# Revit family: Artemide_Vector_PendantMagnetic
name_source: partatom
category: Lighting Fixtures
revit_build: Autodesk Revit 2018 (Build: 20190510_1515(x64)
units: mm (PartAtom-declared; Revit-internal decimal feet)

## family parameters
Always vertical = Yes
Cut with Voids When Loaded = No
Light Source = No
Part Type = Normal
Room Calculation Point = No
Round Connector Dimension = Use Diameter
Shared = No
Work Plane-Based = Yes

## types (135) — shared parameters
6 Monthly = -
Air Handling = -
Annually = -
Application Environment = Internal
Beam Angle Longditudinal Axis  = 0.00°
Beam Angle Transverse Axis  = 0.00°
Bespoke Timeframe = -
CE Approval = Y
Cable Material = -
Colour Rendering Index = 90
Column = -
Control Gear Location = -
Control Gear Required = -
Control Gear Type = -
Daily = -
Daylight Sensor = -
Default Elevation = 1219 mm
Diffuser Finish = -
Diffuser Material  = -
Diffusing screen = -
Distance_HeightTrack = 19 mm
Distance_LeftEndTrack = 54 mm
Distance_RightEnd Track = 54 mm
Distance_WidthTrack = 24 mm
ENEC Certification of European conformity = N
Earth Point  = -
Emergency = N
Emergency Lighting Battery = -
End Caps/Transition Caps/Joints = -
Environmental Product Declaration = -
Expected Life = -
Face Shape = Cylindrical
Features = -
Fire Rated = -
Fire Shroud = -
Fixing Material = -
Fixings = -
Gasket Material = -
Green Guide for Specification = -
Hazardous Area Category = -
Hazardous Area Protection Type = -
Housing Finish  = Painted
Housing Material = Aluminum
IES Files  = -
IK Rating = -
IP Rating = IP20
IfcExportAs = IfcLightFixtureType
IfcExportType = NOT DEFINED
Infills = -
Integral Emergency Lighting Battery Type = -
Integral Fuse or Circuit Protection  = -
Intended Market = Unset
International Type Code = -
Lamp Cap = LED Integrated
Lamp Holder Material = -
Lamp Included = Y
Lamp Replacement Interval = -
Lamp Survival Factor = -
Life Cycle Analysis = -
Light Fixture Mounting Type = Suspended
Light Output Pattern = -
Location of Manufacturer = -
Louvre/Lens = -
Luminaire Cleaning Interval  = -
Luminaire Type = Floodlight
M_Diffuser = Artemide_Glass_LightBulb
Maintenance Required: 0-300hrs  = -
Maintenance Required: 1001-2000hrs  = -
Maintenance Required: 2001-4000hrs  = -
Maintenance Required: 301-600hrs  = -
Maintenance Required: 4001-8000hrs  = -
Maintenance Required: 601-1000hrs = -
Maintenance Required: 8001-12000hrs  = -
Manufacturer = Artemide
Manufacturer Website = https://www.artemide.com
Material Ingredient Reporting = -
Max Height from ceiling = 2000 mm  [stored 6.56168 ft]
Monthly = -
Motion Detector = -
Motion Sensor = -
Number of Primary Lamps = 1
Photocell = -
Power Supply Kit = -
Primary Lamp Type = LED
Product Literature = https://www.artemide.com
Product Range = Vector
Quarterly = -
Reflector Finish = -
Reflector Material = -
Responsible Extraction of Materials = -
Responsible Sourcing of Materials = -
Secondary Lamp = N
Secondary Lamp Cap = -
Secondary Lamp Included = -
Secondary Lamp International Type Code = -
Service life  = -
Standards = -
Suitable Dimmer Type = DALI
Suitable for Dimming  = Y
Suitable for Motion Detector Control = N
Suitable for Photocell Control = -
Testing method = -
Trim Colour  = -
Trim Finish = -
Trim Material = -
URL to Energy Technology List = -
URL to O&M Manual = -
Uniclass 2015 = Pr_70_70_48
Unified Glare Rating  = -
Voltage = -
Warranty ID = https://cloud.artemide.com
Weekly = -
zero-valued in all types: Access Clearance Bottom, Access Clearance Front, Access Clearance Left, Access Clearance Rear, Access Clearance Right, Access Clearance Top, Ambient Temperature                            , Basis of lifetime lumen depreciation  , Basis of lifetime luminaire failures       , Control Gear Standby Power , Current , Cut Out Length, Cut Out Width, Downward Component, Drive Current                                         , Duration of Integral Emergency Lighting , Efficiency, Embodied Carbon , Emergency Charging Power      , Emergency light output percentage, External Control Line Voltage, Face Length, Face Width, Fire Rated Temperature, Fire Rating Duration, Frequency , Gross Weight, Input Lumens Direct light, Input Lumens Indirect light, LED Initial Colour Variation                     , LED Maintained Colour Variation        , LED lifetime, Luminaire Maintenance Factor, Luminance at 65deg Angle, Maximum Operating Temperature, Minimum Operating Temperature, Number of Poles, Number of Secondary Lamps, Output Lumens Indirect light, Overall Light Output Ratio, Overall Width, Power Factor, Secondary Lamp Colour Rendering Index, Secondary Lamp Colour Temperature, Secondary Lamp Efficacy, Secondary Lamp Initial Lumens , Secondary Lamp Voltage, Secondary Rated Lamp Life, Shipping Weight, Supply Phase, Total Light Output , Total Power, Upward Component 

## per-type parameters (varying)
| type | Colour Temperature | Distance_HeightLamp | Housing Colour  | Initial Lumens | M_Fixings | M_Housing | M_TopCap | M_Track | Output Lumens Direct light | Overall Height | Overall Length | Product Model Number | Radius_Lamp | Rated Lamp Life | Wattage  |
| Vector_PendantMagnetic_30_16°_2700K_DALI_BrushedSilver_BN31115 | 2700 | 79 mm | Brushed Silver | 422 | Artemide_Aluminum_Black | Artemide_Aluminum_BrushedSilver | Artemide_Aluminum_BrushedSilver | Artemide_Aluminum_Black | 422 | 78 | 30 | BN31115 | 15 mm  [stored 0.0492126 ft] | 60500 | 6 |
| Vector_PendantMagnetic_40_13°_2700K_DALI_BrushedSilver_AP21115 | 2700 | 105 mm | Brushed Silver | 540 | Artemide_Aluminum_Black | Artemide_Aluminum_BrushedSilver | Artemide_Aluminum_BrushedSilver | Artemide_Aluminum_Black | 540 | 104 | 40 | AP21115 | 20 mm  [stored 0.0656168 ft] | 60500 | 10 |
| Vector_PendantMagnetic_55_16°_2700K_DALI_BrushedSilver_AP31115 | 2700 | 132 mm | Brushed Silver | 1492 | Artemide_Aluminum_Black | Artemide_Aluminum_BrushedSilver | Artemide_Aluminum_BrushedSilver | Artemide_Aluminum_Black | 1492 | 130 | 55 | AP31115 | 28 mm | 50000 | 26 |
| Vector_PendantMagnetic_30_16°_3000K_DALI_BrushedSilver_BN30115 | 3000 | 79 mm | Brushed Silver | 422 | Artemide_Aluminum_Black | Artemide_Aluminum_BrushedSilver | Artemide_Aluminum_BrushedSilver | Artemide_Aluminum_Black | 422 | 78 | 30 | BN30115 | 15 mm  [stored 0.0492126 ft] | 60500 | 6 |
| Vector_PendantMagnetic_30_16°_4000K_DALI_BrushedSilver_BN35115 | 4000 | 79 mm | Brushed Silver | 422 | Artemide_Aluminum_Black | Artemide_Aluminum_BrushedSilver | Artemide_Aluminum_BrushedSilver | Artemide_Aluminum_Black | 422 | 78 | 30 | BN35115 | 15 mm  [stored 0.0492126 ft] | 60500 | 6 |
| Vector_PendantMagnetic_30_20°_2700K_DALI_BrushedSilver_BN31215 | 2700 | 79 mm | Brushed Silver | 404 | Artemide_Aluminum_Black | Artemide_Aluminum_BrushedSilver | Artemide_Aluminum_BrushedSilver | Artemide_Aluminum_Black | 404 | 78 | 30 | BN31215 | 15 mm  [stored 0.0492126 ft] | 60500 | 6 |
| Vector_PendantMagnetic_30_20°_3000K_DALI_BrushedSilver_BN30215 | 3000 | 79 mm | Brushed Silver | 404 | Artemide_Aluminum_Black | Artemide_Aluminum_BrushedSilver | Artemide_Aluminum_BrushedSilver | Artemide_Aluminum_Black | 404 | 78 | 30 | BN30215 | 15 mm  [stored 0.0492126 ft] | 60500 | 6 |
| Vector_PendantMagnetic_30_20°_4000K_DALI_BrushedSilver_BN35215 | 4000 | 79 mm | Brushed Silver | 404 | Artemide_Aluminum_Black | Artemide_Aluminum_BrushedSilver | Artemide_Aluminum_BrushedSilver | Artemide_Aluminum_Black | 404 | 78 | 30 | BN35215 | 15 mm  [stored 0.0492126 ft] | 60500 | 6 |
| Vector_PendantMagnetic_30_28°_2700K_DALI_BrushedSilver_BN31315 | 2700 | 79 mm | Brushed Silver | 373 | Artemide_Aluminum_Black | Artemide_Aluminum_BrushedSilver | Artemide_Aluminum_BrushedSilver | Artemide_Aluminum_Black | 373 | 78 | 30 | BN31315 | 15 mm  [stored 0.0492126 ft] | 60500 | 6 |
| Vector_PendantMagnetic_30_28°_3000K_DALI_BrushedSilver_BN30315 | 3000 | 79 mm | Brushed Silver | 373 | Artemide_Aluminum_Black | Artemide_Aluminum_BrushedSilver | Artemide_Aluminum_BrushedSilver | Artemide_Aluminum_Black | 373 | 78 | 30 | BN30315 | 15 mm  [stored 0.0492126 ft] | 60500 | 6 |
| Vector_PendantMagnetic_30_28°_4000K_DALI_BrushedSilver_BN35315 | 4000 | 79 mm | Brushed Silver | 373 | Artemide_Aluminum_Black | Artemide_Aluminum_BrushedSilver | Artemide_Aluminum_BrushedSilver | Artemide_Aluminum_Black | 373 | 78 | 30 | BN35315 | 15 mm  [stored 0.0492126 ft] | 60500 | 6 |
| Vector_PendantMagnetic_30_16°_2700K_DALI_White_BN31101 | 2700 | 79 mm | White | 422 | Artemide_Aluminum_White | Artemide_Aluminum_White | Artemide_Aluminum_White | Artemide_Aluminum_White | 422 | 78 | 30 | BN31101 | 15 mm  [stored 0.0492126 ft] | 60500 | 6 |
| Vector_PendantMagnetic_30_16°_3000K_DALI_White_BN30101 | 3000 | 79 mm | White | 422 | Artemide_Aluminum_White | Artemide_Aluminum_White | Artemide_Aluminum_White | Artemide_Aluminum_White | 422 | 78 | 30 | BN30101 | 15 mm  [stored 0.0492126 ft] | 60500 | 6 |
| Vector_PendantMagnetic_30_16°_4000K_DALI_White_BN35101 | 4000 | 79 mm | White | 422 | Artemide_Aluminum_White | Artemide_Aluminum_White | Artemide_Aluminum_White | Artemide_Aluminum_White | 422 | 78 | 30 | BN35101 | 15 mm  [stored 0.0492126 ft] | 60500 | 6 |
| Vector_PendantMagnetic_30_20°_2700K_DALI_White_BN31201 | 2700 | 79 mm | White | 404 | Artemide_Aluminum_White | Artemide_Aluminum_White | Artemide_Aluminum_White | Artemide_Aluminum_White | 404 | 78 | 30 | BN31201 | 15 mm  [stored 0.0492126 ft] | 60500 | 6 |
| Vector_PendantMagnetic_30_20°_3000K_DALI_White_BN30201 | 3000 | 79 mm | White | 404 | Artemide_Aluminum_White | Artemide_Aluminum_White | Artemide_Aluminum_White | Artemide_Aluminum_White | 404 | 78 | 30 | BN30201 | 15 mm  [stored 0.0492126 ft] | 60500 | 6 |
| Vector_PendantMagnetic_30_20°_4000K_DALI_White_BN35201 | 4000 | 79 mm | White | 404 | Artemide_Aluminum_White | Artemide_Aluminum_White | Artemide_Aluminum_White | Artemide_Aluminum_White | 404 | 78 | 30 | BN35201 | 15 mm  [stored 0.0492126 ft] | 60500 | 6 |
| Vector_PendantMagnetic_30_28°_2700K_DALI_White_BN31301 | 2700 | 79 mm | White | 373 | Artemide_Aluminum_White | Artemide_Aluminum_White | Artemide_Aluminum_White | Artemide_Aluminum_White | 373 | 78 | 30 | BN31301 | 15 mm  [stored 0.0492126 ft] | 60500 | 6 |
| Vector_PendantMagnetic_30_28°_3000K_DALI_White_BN30301 | 3000 | 79 mm | White | 373 | Artemide_Aluminum_White | Artemide_Aluminum_White | Artemide_Aluminum_White | Artemide_Aluminum_White | 373 | 78 | 30 | BN30301 | 15 mm  [stored 0.0492126 ft] | 60500 | 6 |
| Vector_PendantMagnetic_30_28°_4000K_DALI_White_BN35301 | 4000 | 79 mm | White | 373 | Artemide_Aluminum_White | Artemide_Aluminum_White | Artemide_Aluminum_White | Artemide_Aluminum_White | 373 | 78 | 30 | BN35301 | 15 mm  [stored 0.0492126 ft] | 60500 | 6 |
| Vector_PendantMagnetic_30_16°_2700K_DALI_BrushedBronze_BN31120 | 2700 | 79 mm | Brushed Bronze | 422 | Artemide_Aluminum_Black | Artemide_Aluminum_BrushedBronze | Artemide_Aluminum_BrushedBronze | Artemide_Aluminum_Black | 422 | 78 | 30 | BN31120 | 15 mm  [stored 0.0492126 ft] | 60500 | 6 |
| Vector_PendantMagnetic_30_16°_3000K_DALI_BrushedBronze_BN30120 | 3000 | 79 mm | Brushed Bronze | 422 | Artemide_Aluminum_Black | Artemide_Aluminum_BrushedBronze | Artemide_Aluminum_BrushedBronze | Artemide_Aluminum_Black | 422 | 78 | 30 | BN30120 | 15 mm  [stored 0.0492126 ft] | 60500 | 6 |
| Vector_PendantMagnetic_30_16°_4000K_DALI_BrushedBronze_BN35120 | 4000 | 79 mm | Brushed Bronze | 422 | Artemide_Aluminum_Black | Artemide_Aluminum_BrushedBronze | Artemide_Aluminum_BrushedBronze | Artemide_Aluminum_Black | 422 | 78 | 30 | BN35120 | 15 mm  [stored 0.0492126 ft] | 60500 | 6 |
| Vector_PendantMagnetic_30_20°_2700K_DALI_BrushedBronze_BN31220 | 2700 | 79 mm | Brushed Bronze | 404 | Artemide_Aluminum_Black | Artemide_Aluminum_BrushedBronze | Artemide_Aluminum_BrushedBronze | Artemide_Aluminum_Black | 404 | 78 | 30 | BN31220 | 15 mm  [stored 0.0492126 ft] | 60500 | 6 |
| Vector_PendantMagnetic_30_20°_3000K_DALI_BrushedBronze_BN30220 | 3000 | 79 mm | Brushed Bronze | 404 | Artemide_Aluminum_Black | Artemide_Aluminum_BrushedBronze | Artemide_Aluminum_BrushedBronze | Artemide_Aluminum_Black | 404 | 78 | 30 | BN30220 | 15 mm  [stored 0.0492126 ft] | 60500 | 6 |
| Vector_PendantMagnetic_30_20°_4000K_DALI_BrushedBronze_BN35220 | 4000 | 79 mm | Brushed Bronze | 404 | Artemide_Aluminum_Black | Artemide_Aluminum_BrushedBronze | Artemide_Aluminum_BrushedBronze | Artemide_Aluminum_Black | 404 | 78 | 30 | BN35220 | 15 mm  [stored 0.0492126 ft] | 60500 | 6 |
| Vector_PendantMagnetic_30_28°_2700K_DALI_BrushedBronze_BN31320 | 2700 | 79 mm | Brushed Bronze | 373 | Artemide_Aluminum_Black | Artemide_Aluminum_BrushedBronze | Artemide_Aluminum_BrushedBronze | Artemide_Aluminum_Black | 373 | 78 | 30 | BN31320 | 15 mm  [stored 0.0492126 ft] | 60500 | 6 |
| Vector_PendantMagnetic_30_28°_3000K_DALI_BrushedBronze_BN30320 | 3000 | 79 mm | Brushed Bronze | 373 | Artemide_Aluminum_Black | Artemide_Aluminum_BrushedBronze | Artemide_Aluminum_BrushedBronze | Artemide_Aluminum_Black | 373 | 78 | 30 | BN30320 | 15 mm  [stored 0.0492126 ft] | 60500 | 6 |
| Vector_PendantMagnetic_30_28°_4000K_DALI_BrushedBronze_BN35320 | 4000 | 79 mm | Brushed Bronze | 373 | Artemide_Aluminum_Black | Artemide_Aluminum_BrushedBronze | Artemide_Aluminum_BrushedBronze | Artemide_Aluminum_Black | 373 | 78 | 30 | BN35320 | 15 mm  [stored 0.0492126 ft] | 60500 | 6 |
| Vector_PendantMagnetic_30_16°_2700K_DALI_Black_BN31104 | 2700 | 79 mm | Black | 422 | Artemide_Aluminum_Black | Artemide_Aluminum_Black | Artemide_Aluminum_Black | Artemide_Aluminum_Black | 422 | 78 | 30 | BN31104 | 15 mm  [stored 0.0492126 ft] | 60500 | 6 |
| Vector_PendantMagnetic_30_16°_3000K_DALI_Black_BN30104 | 3000 | 79 mm | Black | 422 | Artemide_Aluminum_Black | Artemide_Aluminum_Black | Artemide_Aluminum_Black | Artemide_Aluminum_Black | 422 | 78 | 30 | BN30104 | 15 mm  [stored 0.0492126 ft] | 60500 | 6 |
| Vector_PendantMagnetic_30_16°_4000K_DALI_Black_BN35104 | 4000 | 79 mm | Black | 422 | Artemide_Aluminum_Black | Artemide_Aluminum_Black | Artemide_Aluminum_Black | Artemide_Aluminum_Black | 422 | 78 | 30 | BN35104 | 15 mm  [stored 0.0492126 ft] | 60500 | 6 |
| Vector_PendantMagnetic_30_20°_2700K_DALI_Black_BN31204 | 2700 | 79 mm | Black | 404 | Artemide_Aluminum_Black | Artemide_Aluminum_Black | Artemide_Aluminum_Black | Artemide_Aluminum_Black | 404 | 78 | 30 | BN31204 | 15 mm  [stored 0.0492126 ft] | 60500 | 6 |
| Vector_PendantMagnetic_30_20°_3000K_DALI_Black_BN30204 | 3000 | 79 mm | Black | 404 | Artemide_Aluminum_Black | Artemide_Aluminum_Black | Artemide_Aluminum_Black | Artemide_Aluminum_Black | 404 | 78 | 30 | BN30204 | 15 mm  [stored 0.0492126 ft] | 60500 | 6 |
| Vector_PendantMagnetic_30_20°_4000K_DALI_Black_BN35204 | 4000 | 79 mm | Black | 404 | Artemide_Aluminum_Black | Artemide_Aluminum_Black | Artemide_Aluminum_Black | Artemide_Aluminum_Black | 404 | 78 | 30 | BN35204 | 15 mm  [stored 0.0492126 ft] | 60500 | 6 |
| Vector_PendantMagnetic_30_28°_2700K_DALI_Black_BN31304 | 2700 | 79 mm | Black | 373 | Artemide_Aluminum_Black | Artemide_Aluminum_Black | Artemide_Aluminum_Black | Artemide_Aluminum_Black | 373 | 78 | 30 | BN31304 | 15 mm  [stored 0.0492126 ft] | 60500 | 6 |
| Vector_PendantMagnetic_30_28°_3000K_DALI_Black_BN30304 | 3000 | 79 mm | Black | 373 | Artemide_Aluminum_Black | Artemide_Aluminum_Black | Artemide_Aluminum_Black | Artemide_Aluminum_Black | 373 | 78 | 30 | BN30304 | 15 mm  [stored 0.0492126 ft] | 60500 | 6 |
| Vector_PendantMagnetic_30_28°_4000K_DALI_Black_BN35304 | 4000 | 79 mm | Black | 373 | Artemide_Aluminum_Black | Artemide_Aluminum_Black | Artemide_Aluminum_Black | Artemide_Aluminum_Black | 373 | 78 | 30 | BN35304 | 15 mm  [stored 0.0492126 ft] | 60500 | 6 |
| Vector_PendantMagnetic_30_16°_2700K_DALI_BrushedCopper_BN31118 | 2700 | 79 mm | Brushed Copper | 422 | Artemide_Aluminum_Black | Artemide_Aluminum_BrushedCopper | Artemide_Aluminum_BrushedCopper | Artemide_Aluminum_Black | 422 | 78 | 30 | BN31118 | 15 mm  [stored 0.0492126 ft] | 60500 | 6 |
| Vector_PendantMagnetic_30_16°_3000K_DALI_BrushedCopper_BN30118 | 3000 | 79 mm | Brushed Copper | 422 | Artemide_Aluminum_Black | Artemide_Aluminum_BrushedCopper | Artemide_Aluminum_BrushedCopper | Artemide_Aluminum_Black | 422 | 78 | 30 | BN30118 | 15 mm  [stored 0.0492126 ft] | 60500 | 6 |
| Vector_PendantMagnetic_30_16°_4000K_DALI_BrushedCopper_BN35118 | 4000 | 79 mm | Brushed Copper | 422 | Artemide_Aluminum_Black | Artemide_Aluminum_BrushedCopper | Artemide_Aluminum_BrushedCopper | Artemide_Aluminum_Black | 422 | 78 | 30 | BN35118 | 15 mm  [stored 0.0492126 ft] | 60500 | 6 |
| Vector_PendantMagnetic_30_20°_2700K_DALI_BrushedCopper_BN31218 | 2700 | 79 mm | Brushed Copper | 404 | Artemide_Aluminum_Black | Artemide_Aluminum_BrushedCopper | Artemide_Aluminum_BrushedCopper | Artemide_Aluminum_Black | 404 | 78 | 30 | BN31218 | 15 mm  [stored 0.0492126 ft] | 60500 | 6 |
| Vector_PendantMagnetic_30_20°_3000K_DALI_BrushedCopper_BN30218 | 3000 | 79 mm | Brushed Copper | 404 | Artemide_Aluminum_Black | Artemide_Aluminum_BrushedCopper | Artemide_Aluminum_BrushedCopper | Artemide_Aluminum_Black | 404 | 78 | 30 | BN30218 | 15 mm  [stored 0.0492126 ft] | 60500 | 6 |
| Vector_PendantMagnetic_30_20°_4000K_DALI_BrushedCopper_BN35218 | 4000 | 79 mm | Brushed Copper | 404 | Artemide_Aluminum_Black | Artemide_Aluminum_BrushedCopper | Artemide_Aluminum_BrushedCopper | Artemide_Aluminum_Black | 404 | 78 | 30 | BN35218 | 15 mm  [stored 0.0492126 ft] | 60500 | 6 |
| Vector_PendantMagnetic_30_28°_2700K_DALI_BrushedCopper_BN31318 | 2700 | 79 mm | Brushed Copper | 373 | Artemide_Aluminum_Black | Artemide_Aluminum_BrushedCopper | Artemide_Aluminum_BrushedCopper | Artemide_Aluminum_Black | 373 | 78 | 30 | BN31318 | 15 mm  [stored 0.0492126 ft] | 60500 | 6 |
| Vector_PendantMagnetic_30_28°_3000K_DALI_BrushedCopper_BN30318 | 3000 | 79 mm | Brushed Copper | 373 | Artemide_Aluminum_Black | Artemide_Aluminum_BrushedCopper | Artemide_Aluminum_BrushedCopper | Artemide_Aluminum_Black | 373 | 78 | 30 | BN30318 | 15 mm  [stored 0.0492126 ft] | 60500 | 6 |
| Vector_PendantMagnetic_30_28°_4000K_DALI_BrushedCopper_BN35318 | 4000 | 79 mm | Brushed Copper | 373 | Artemide_Aluminum_Black | Artemide_Aluminum_BrushedCopper | Artemide_Aluminum_BrushedCopper | Artemide_Aluminum_Black | 373 | 78 | 30 | BN35318 | 15 mm  [stored 0.0492126 ft] | 60500 | 6 |
| Vector_PendantMagnetic_40_13°_3000K_DALI_BrushedSilver_AP20115 | 3000 | 105 mm | Brushed Silver | 540 | Artemide_Aluminum_Black | Artemide_Aluminum_BrushedSilver | Artemide_Aluminum_BrushedSilver | Artemide_Aluminum_Black | 540 | 104 | 40 | AP20115 | 20 mm  [stored 0.0656168 ft] | 60500 | 10 |
| Vector_PendantMagnetic_40_13°_4000K_DALI_BrushedSilver_AP25115 | 4000 | 105 mm | Brushed Silver | 540 | Artemide_Aluminum_Black | Artemide_Aluminum_BrushedSilver | Artemide_Aluminum_BrushedSilver | Artemide_Aluminum_Black | 540 | 104 | 40 | AP25115 | 20 mm  [stored 0.0656168 ft] | 60500 | 10 |
| Vector_PendantMagnetic_40_20°_2700K_DALI_BrushedSilver_AP21215 | 2700 | 105 mm | Brushed Silver | 584 | Artemide_Aluminum_Black | Artemide_Aluminum_BrushedSilver | Artemide_Aluminum_BrushedSilver | Artemide_Aluminum_Black | 584 | 104 | 40 | AP21215 | 20 mm  [stored 0.0656168 ft] | 60500 | 10 |
| Vector_PendantMagnetic_40_20°_3000K_DALI_BrushedSilver_AP20215 | 3000 | 105 mm | Brushed Silver | 584 | Artemide_Aluminum_Black | Artemide_Aluminum_BrushedSilver | Artemide_Aluminum_BrushedSilver | Artemide_Aluminum_Black | 584 | 104 | 40 | AP20215 | 20 mm  [stored 0.0656168 ft] | 60500 | 10 |
| Vector_PendantMagnetic_40_20°_4000K_DALI_BrushedSilver_AP25215 | 4000 | 105 mm | Brushed Silver | 584 | Artemide_Aluminum_Black | Artemide_Aluminum_BrushedSilver | Artemide_Aluminum_BrushedSilver | Artemide_Aluminum_Black | 584 | 104 | 40 | AP25215 | 20 mm  [stored 0.0656168 ft] | 60500 | 10 |
| Vector_PendantMagnetic_40_28°_2700K_DALI_BrushedSilver_AP21315 | 2700 | 105 mm | Brushed Silver | 528 | Artemide_Aluminum_Black | Artemide_Aluminum_BrushedSilver | Artemide_Aluminum_BrushedSilver | Artemide_Aluminum_Black | 528 | 104 | 40 | AP21315 | 20 mm  [stored 0.0656168 ft] | 60500 | 10 |
| Vector_PendantMagnetic_40_28°_3000K_DALI_BrushedSilver_AP20315 | 3000 | 105 mm | Brushed Silver | 528 | Artemide_Aluminum_Black | Artemide_Aluminum_BrushedSilver | Artemide_Aluminum_BrushedSilver | Artemide_Aluminum_Black | 528 | 104 | 40 | AP20315 | 20 mm  [stored 0.0656168 ft] | 60500 | 10 |
| Vector_PendantMagnetic_40_28°_4000K_DALI_BrushedSilver_AP25315 | 4000 | 105 mm | Brushed Silver | 528 | Artemide_Aluminum_Black | Artemide_Aluminum_BrushedSilver | Artemide_Aluminum_BrushedSilver | Artemide_Aluminum_Black | 528 | 104 | 40 | AP25315 | 20 mm  [stored 0.0656168 ft] | 60500 | 10 |
| Vector_PendantMagnetic_40_13°_2700K_DALI_White_AP21101 | 2700 | 105 mm | White | 540 | Artemide_Aluminum_White | Artemide_Aluminum_White | Artemide_Aluminum_White | Artemide_Aluminum_White | 540 | 104 | 40 | AP21101 | 20 mm  [stored 0.0656168 ft] | 60500 | 10 |
| Vector_PendantMagnetic_40_13°_3000K_DALI_White_AP20101 | 3000 | 105 mm | White | 540 | Artemide_Aluminum_White | Artemide_Aluminum_White | Artemide_Aluminum_White | Artemide_Aluminum_White | 540 | 104 | 40 | AP20101 | 20 mm  [stored 0.0656168 ft] | 60500 | 10 |
| Vector_PendantMagnetic_40_13°_4000K_DALI_White_AP25101 | 4000 | 105 mm | White | 540 | Artemide_Aluminum_White | Artemide_Aluminum_White | Artemide_Aluminum_White | Artemide_Aluminum_White | 540 | 104 | 40 | AP25101 | 20 mm  [stored 0.0656168 ft] | 60500 | 10 |
| Vector_PendantMagnetic_40_20°_2700K_DALI_White_AP21201 | 2700 | 105 mm | White | 584 | Artemide_Aluminum_White | Artemide_Aluminum_White | Artemide_Aluminum_White | Artemide_Aluminum_White | 584 | 104 | 40 | AP21201 | 20 mm  [stored 0.0656168 ft] | 60500 | 10 |
| Vector_PendantMagnetic_40_20°_3000K_DALI_White_AP20201 | 3000 | 105 mm | White | 584 | Artemide_Aluminum_White | Artemide_Aluminum_White | Artemide_Aluminum_White | Artemide_Aluminum_White | 584 | 104 | 40 | AP20201 | 20 mm  [stored 0.0656168 ft] | 60500 | 10 |
| Vector_PendantMagnetic_40_20°_4000K_DALI_White_AP25201 | 4000 | 105 mm | White | 584 | Artemide_Aluminum_White | Artemide_Aluminum_White | Artemide_Aluminum_White | Artemide_Aluminum_White | 584 | 104 | 40 | AP25201 | 20 mm  [stored 0.0656168 ft] | 60500 | 10 |
| Vector_PendantMagnetic_40_28°_2700K_DALI_White_AP21301 | 2700 | 105 mm | White | 528 | Artemide_Aluminum_White | Artemide_Aluminum_White | Artemide_Aluminum_White | Artemide_Aluminum_White | 528 | 104 | 40 | AP21301 | 20 mm  [stored 0.0656168 ft] | 60500 | 10 |
| Vector_PendantMagnetic_40_28°_3000K_DALI_White_AP20301 | 3000 | 105 mm | White | 528 | Artemide_Aluminum_White | Artemide_Aluminum_White | Artemide_Aluminum_White | Artemide_Aluminum_White | 528 | 104 | 40 | AP20301 | 20 mm  [stored 0.0656168 ft] | 60500 | 10 |
| Vector_PendantMagnetic_40_28°_4000K_DALI_White_AP25301 | 4000 | 105 mm | White | 528 | Artemide_Aluminum_White | Artemide_Aluminum_White | Artemide_Aluminum_White | Artemide_Aluminum_White | 528 | 104 | 40 | AP25301 | 20 mm  [stored 0.0656168 ft] | 60500 | 10 |
| Vector_PendantMagnetic_40_13°_2700K_DALI_BrushedBronze_AP21120 | 2700 | 105 mm | Brushed Bronze | 540 | Artemide_Aluminum_Black | Artemide_Aluminum_BrushedBronze | Artemide_Aluminum_BrushedBronze | Artemide_Aluminum_Black | 540 | 104 | 40 | AP21120 | 20 mm  [stored 0.0656168 ft] | 60500 | 10 |
| Vector_PendantMagnetic_40_13°_3000K_DALI_BrushedBronze_AP20120 | 3000 | 105 mm | Brushed Bronze | 540 | Artemide_Aluminum_Black | Artemide_Aluminum_BrushedBronze | Artemide_Aluminum_BrushedBronze | Artemide_Aluminum_Black | 540 | 104 | 40 | AP20120 | 20 mm  [stored 0.0656168 ft] | 60500 | 10 |
| Vector_PendantMagnetic_40_13°_4000K_DALI_BrushedBronze_AP25120 | 4000 | 105 mm | Brushed Bronze | 540 | Artemide_Aluminum_Black | Artemide_Aluminum_BrushedBronze | Artemide_Aluminum_BrushedBronze | Artemide_Aluminum_Black | 540 | 104 | 40 | AP25120 | 20 mm  [stored 0.0656168 ft] | 60500 | 10 |
| Vector_PendantMagnetic_40_20°_2700K_DALI_BrushedBronze_AP21220 | 2700 | 105 mm | Brushed Bronze | 584 | Artemide_Aluminum_Black | Artemide_Aluminum_BrushedBronze | Artemide_Aluminum_BrushedBronze | Artemide_Aluminum_Black | 584 | 104 | 40 | AP21220 | 20 mm  [stored 0.0656168 ft] | 60500 | 10 |
| Vector_PendantMagnetic_40_20°_3000K_DALI_BrushedBronze_AP20220 | 3000 | 105 mm | Brushed Bronze | 584 | Artemide_Aluminum_Black | Artemide_Aluminum_BrushedBronze | Artemide_Aluminum_BrushedBronze | Artemide_Aluminum_Black | 584 | 104 | 40 | AP20220 | 20 mm  [stored 0.0656168 ft] | 60500 | 10 |
| Vector_PendantMagnetic_40_20°_4000K_DALI_BrushedBronze_AP25220 | 4000 | 105 mm | Brushed Bronze | 584 | Artemide_Aluminum_Black | Artemide_Aluminum_BrushedBronze | Artemide_Aluminum_BrushedBronze | Artemide_Aluminum_Black | 584 | 104 | 40 | AP25220 | 20 mm  [stored 0.0656168 ft] | 60500 | 10 |
| Vector_PendantMagnetic_40_28°_2700K_DALI_BrushedBronze_AP21320 | 2700 | 105 mm | Brushed Bronze | 528 | Artemide_Aluminum_Black | Artemide_Aluminum_BrushedBronze | Artemide_Aluminum_BrushedBronze | Artemide_Aluminum_Black | 528 | 104 | 40 | AP21320 | 20 mm  [stored 0.0656168 ft] | 60500 | 10 |
| Vector_PendantMagnetic_40_28°_3000K_DALI_BrushedBronze_AP20320 | 3000 | 105 mm | Brushed Bronze | 528 | Artemide_Aluminum_Black | Artemide_Aluminum_BrushedBronze | Artemide_Aluminum_BrushedBronze | Artemide_Aluminum_Black | 528 | 104 | 40 | AP20320 | 20 mm  [stored 0.0656168 ft] | 60500 | 10 |
| Vector_PendantMagnetic_40_28°_4000K_DALI_BrushedBronze_AP25320 | 4000 | 105 mm | Brushed Bronze | 528 | Artemide_Aluminum_Black | Artemide_Aluminum_BrushedBronze | Artemide_Aluminum_BrushedBronze | Artemide_Aluminum_Black | 528 | 104 | 40 | AP25320 | 20 mm  [stored 0.0656168 ft] | 60500 | 10 |
| Vector_PendantMagnetic_40_13°_2700K_DALI_Black_AP21104 | 2700 | 105 mm | Black | 540 | Artemide_Aluminum_Black | Artemide_Aluminum_Black | Artemide_Aluminum_Black | Artemide_Aluminum_Black | 540 | 104 | 40 | AP21104 | 20 mm  [stored 0.0656168 ft] | 60500 | 10 |
| Vector_PendantMagnetic_40_13°_3000K_DALI_Black_AP20104 | 3000 | 105 mm | Black | 540 | Artemide_Aluminum_Black | Artemide_Aluminum_Black | Artemide_Aluminum_Black | Artemide_Aluminum_Black | 540 | 104 | 40 | AP20104 | 20 mm  [stored 0.0656168 ft] | 60500 | 10 |
| Vector_PendantMagnetic_40_13°_4000K_DALI_Black_AP25104 | 4000 | 105 mm | Black | 540 | Artemide_Aluminum_Black | Artemide_Aluminum_Black | Artemide_Aluminum_Black | Artemide_Aluminum_Black | 540 | 104 | 40 | AP25104 | 20 mm  [stored 0.0656168 ft] | 60500 | 10 |
| Vector_PendantMagnetic_40_20°_2700K_DALI_Black_AP21204 | 2700 | 105 mm | Black | 584 | Artemide_Aluminum_Black | Artemide_Aluminum_Black | Artemide_Aluminum_Black | Artemide_Aluminum_Black | 584 | 104 | 40 | AP21204 | 20 mm  [stored 0.0656168 ft] | 60500 | 10 |
| Vector_PendantMagnetic_40_20°_3000K_DALI_Black_AP20204 | 3000 | 105 mm | Black | 584 | Artemide_Aluminum_Black | Artemide_Aluminum_Black | Artemide_Aluminum_Black | Artemide_Aluminum_Black | 584 | 104 | 40 | AP20204 | 20 mm  [stored 0.0656168 ft] | 60500 | 10 |
| Vector_PendantMagnetic_40_20°_4000K_DALI_Black_AP25204 | 4000 | 105 mm | Black | 584 | Artemide_Aluminum_Black | Artemide_Aluminum_Black | Artemide_Aluminum_Black | Artemide_Aluminum_Black | 584 | 104 | 40 | AP25204 | 20 mm  [stored 0.0656168 ft] | 60500 | 10 |
| Vector_PendantMagnetic_40_28°_2700K_DALI_Black_AP21304 | 2700 | 105 mm | Black | 528 | Artemide_Aluminum_Black | Artemide_Aluminum_Black | Artemide_Aluminum_Black | Artemide_Aluminum_Black | 528 | 104 | 40 | AP21304 | 20 mm  [stored 0.0656168 ft] | 60500 | 10 |
| Vector_PendantMagnetic_40_28°_3000K_DALI_Black_AP20304 | 3000 | 105 mm | Black | 528 | Artemide_Aluminum_Black | Artemide_Aluminum_Black | Artemide_Aluminum_Black | Artemide_Aluminum_Black | 528 | 104 | 40 | AP20304 | 20 mm  [stored 0.0656168 ft] | 60500 | 10 |
| Vector_PendantMagnetic_40_28°_4000K_DALI_Black_AP25304 | 4000 | 105 mm | Black | 528 | Artemide_Aluminum_Black | Artemide_Aluminum_Black | Artemide_Aluminum_Black | Artemide_Aluminum_Black | 528 | 104 | 40 | AP25304 | 20 mm  [stored 0.0656168 ft] | 60500 | 10 |
| Vector_PendantMagnetic_40_13°_2700K_DALI_BrushedCopper_AP21118 | 2700 | 105 mm | Brushed Copper | 540 | Artemide_Aluminum_Black | Artemide_Aluminum_BrushedCopper | Artemide_Aluminum_BrushedCopper | Artemide_Aluminum_Black | 540 | 104 | 40 | AP21118 | 20 mm  [stored 0.0656168 ft] | 60500 | 10 |
| Vector_PendantMagnetic_40_13°_3000K_DALI_BrushedCopper_AP20118 | 3000 | 105 mm | Brushed Copper | 540 | Artemide_Aluminum_Black | Artemide_Aluminum_BrushedCopper | Artemide_Aluminum_BrushedCopper | Artemide_Aluminum_Black | 540 | 104 | 40 | AP20118 | 20 mm  [stored 0.0656168 ft] | 60500 | 10 |
| Vector_PendantMagnetic_40_13°_4000K_DALI_BrushedCopper_AP25118 | 4000 | 105 mm | Brushed Copper | 540 | Artemide_Aluminum_Black | Artemide_Aluminum_BrushedCopper | Artemide_Aluminum_BrushedCopper | Artemide_Aluminum_Black | 540 | 104 | 40 | AP25118 | 20 mm  [stored 0.0656168 ft] | 60500 | 10 |
| Vector_PendantMagnetic_40_20°_2700K_DALI_BrushedCopper_AP21218 | 2700 | 105 mm | Brushed Copper | 584 | Artemide_Aluminum_Black | Artemide_Aluminum_BrushedCopper | Artemide_Aluminum_BrushedCopper | Artemide_Aluminum_Black | 584 | 104 | 40 | AP21218 | 20 mm  [stored 0.0656168 ft] | 60500 | 10 |
| Vector_PendantMagnetic_40_20°_3000K_DALI_BrushedCopper_AP20218 | 3000 | 105 mm | Brushed Copper | 584 | Artemide_Aluminum_Black | Artemide_Aluminum_BrushedCopper | Artemide_Aluminum_BrushedCopper | Artemide_Aluminum_Black | 584 | 104 | 40 | AP20218 | 20 mm  [stored 0.0656168 ft] | 60500 | 10 |
| Vector_PendantMagnetic_40_20°_4000K_DALI_BrushedCopper_AP25218 | 4000 | 105 mm | Brushed Copper | 584 | Artemide_Aluminum_Black | Artemide_Aluminum_BrushedCopper | Artemide_Aluminum_BrushedCopper | Artemide_Aluminum_Black | 584 | 104 | 40 | AP25218 | 20 mm  [stored 0.0656168 ft] | 60500 | 10 |
| Vector_PendantMagnetic_40_28°_2700K_DALI_BrushedCopper_AP21318 | 2700 | 105 mm | Brushed Copper | 528 | Artemide_Aluminum_Black | Artemide_Aluminum_BrushedCopper | Artemide_Aluminum_BrushedCopper | Artemide_Aluminum_Black | 528 | 104 | 40 | AP21318 | 20 mm  [stored 0.0656168 ft] | 60500 | 10 |
| Vector_PendantMagnetic_40_28°_3000K_DALI_BrushedCopper_AP20318 | 3000 | 105 mm | Brushed Copper | 528 | Artemide_Aluminum_Black | Artemide_Aluminum_BrushedCopper | Artemide_Aluminum_BrushedCopper | Artemide_Aluminum_Black | 528 | 104 | 40 | AP20318 | 20 mm  [stored 0.0656168 ft] | 60500 | 10 |
| Vector_PendantMagnetic_40_28°_4000K_DALI_BrushedCopper_AP25318 | 4000 | 105 mm | Brushed Copper | 528 | Artemide_Aluminum_Black | Artemide_Aluminum_BrushedCopper | Artemide_Aluminum_BrushedCopper | Artemide_Aluminum_Black | 528 | 104 | 40 | AP25318 | 20 mm  [stored 0.0656168 ft] | 60500 | 10 |
| Vector_PendantMagnetic_55_16°_3000K_DALI_BrushedSilver_AP30115 | 3000 | 132 mm | Brushed Silver | 1492 | Artemide_Aluminum_Black | Artemide_Aluminum_BrushedSilver | Artemide_Aluminum_BrushedSilver | Artemide_Aluminum_Black | 1492 | 130 | 55 | AP30115 | 28 mm | 50000 | 26 |
| Vector_PendantMagnetic_55_16°_4000K_DALI_BrushedSilver_AP35115 | 4000 | 132 mm | Brushed Silver | 1492 | Artemide_Aluminum_Black | Artemide_Aluminum_BrushedSilver | Artemide_Aluminum_BrushedSilver | Artemide_Aluminum_Black | 1492 | 130 | 55 | AP35115 | 28 mm | 50000 | 26 |
| Vector_PendantMagnetic_55_22°_2700K_DALI_BrushedSilver_AP31215 | 2700 | 132 mm | Brushed Silver | 1465 | Artemide_Aluminum_Black | Artemide_Aluminum_BrushedSilver | Artemide_Aluminum_BrushedSilver | Artemide_Aluminum_Black | 1465 | 130 | 55 | AP31215 | 28 mm | 50000 | 26 |
| Vector_PendantMagnetic_55_22°_3000K_DALI_BrushedSilver_AP30215 | 3000 | 132 mm | Brushed Silver | 1465 | Artemide_Aluminum_Black | Artemide_Aluminum_BrushedSilver | Artemide_Aluminum_BrushedSilver | Artemide_Aluminum_Black | 1465 | 130 | 55 | AP30215 | 28 mm | 50000 | 26 |
| Vector_PendantMagnetic_55_22°_4000K_DALI_BrushedSilver_AP35215 | 4000 | 132 mm | Brushed Silver | 1465 | Artemide_Aluminum_Black | Artemide_Aluminum_BrushedSilver | Artemide_Aluminum_BrushedSilver | Artemide_Aluminum_Black | 1465 | 130 | 55 | AP35215 | 28 mm | 50000 | 26 |
| Vector_PendantMagnetic_55_32°_2700K_DALI_BrushedSilver_AP31315 | 2700 | 132 mm | Brushed Silver | 1596 | Artemide_Aluminum_Black | Artemide_Aluminum_BrushedSilver | Artemide_Aluminum_BrushedSilver | Artemide_Aluminum_Black | 1596 | 130 | 55 | AP31315 | 28 mm | 50000 | 26 |
| Vector_PendantMagnetic_55_32°_3000K_DALI_BrushedSilver_AP30315 | 3000 | 132 mm | Brushed Silver | 1596 | Artemide_Aluminum_Black | Artemide_Aluminum_BrushedSilver | Artemide_Aluminum_BrushedSilver | Artemide_Aluminum_Black | 1596 | 130 | 55 | AP30315 | 28 mm | 50000 | 26 |
| Vector_PendantMagnetic_55_32°_4000K_DALI_BrushedSilver_AP35315 | 4000 | 132 mm | Brushed Silver | 1596 | Artemide_Aluminum_Black | Artemide_Aluminum_BrushedSilver | Artemide_Aluminum_BrushedSilver | Artemide_Aluminum_Black | 1596 | 130 | 55 | AP35315 | 28 mm | 50000 | 26 |
| Vector_PendantMagnetic_55_16°_2700K_DALI_White_AP31101 | 2700 | 132 mm | White | 1492 | Artemide_Aluminum_White | Artemide_Aluminum_White | Artemide_Aluminum_White | Artemide_Aluminum_White | 1492 | 130 | 55 | AP31101 | 28 mm | 50000 | 26 |
| Vector_PendantMagnetic_55_16°_3000K_DALI_White_AP30101 | 3000 | 132 mm | White | 1492 | Artemide_Aluminum_White | Artemide_Aluminum_White | Artemide_Aluminum_White | Artemide_Aluminum_White | 1492 | 130 | 55 | AP30101 | 28 mm | 50000 | 26 |
| Vector_PendantMagnetic_55_16°_4000K_DALI_White_AP35101 | 4000 | 132 mm | White | 1492 | Artemide_Aluminum_White | Artemide_Aluminum_White | Artemide_Aluminum_White | Artemide_Aluminum_White | 1492 | 130 | 55 | AP35101 | 28 mm | 50000 | 26 |
| Vector_PendantMagnetic_55_22°_2700K_DALI_White_AP31201 | 2700 | 132 mm | White | 1465 | Artemide_Aluminum_White | Artemide_Aluminum_White | Artemide_Aluminum_White | Artemide_Aluminum_White | 1465 | 130 | 55 | AP31201 | 28 mm | 50000 | 26 |
| Vector_PendantMagnetic_55_22°_3000K_DALI_White_AP30201 | 3000 | 132 mm | White | 1465 | Artemide_Aluminum_White | Artemide_Aluminum_White | Artemide_Aluminum_White | Artemide_Aluminum_White | 1465 | 130 | 55 | AP30201 | 28 mm | 50000 | 26 |
| Vector_PendantMagnetic_55_22°_4000K_DALI_White_AP35201 | 4000 | 132 mm | White | 1465 | Artemide_Aluminum_White | Artemide_Aluminum_White | Artemide_Aluminum_White | Artemide_Aluminum_White | 1465 | 130 | 55 | AP35201 | 28 mm | 50000 | 26 |
| Vector_PendantMagnetic_55_32°_2700K_DALI_White_AP31301 | 2700 | 132 mm | White | 1596 | Artemide_Aluminum_White | Artemide_Aluminum_White | Artemide_Aluminum_White | Artemide_Aluminum_White | 1596 | 130 | 55 | AP31301 | 28 mm | 50000 | 26 |
| Vector_PendantMagnetic_55_32°_3000K_DALI_White_AP30301 | 3000 | 132 mm | White | 1596 | Artemide_Aluminum_White | Artemide_Aluminum_White | Artemide_Aluminum_White | Artemide_Aluminum_White | 1596 | 130 | 55 | AP30301 | 28 mm | 50000 | 26 |
| Vector_PendantMagnetic_55_32°_4000K_DALI_White_AP35301 | 4000 | 132 mm | White | 1596 | Artemide_Aluminum_White | Artemide_Aluminum_White | Artemide_Aluminum_White | Artemide_Aluminum_White | 1596 | 130 | 55 | AP35301 | 28 mm | 50000 | 26 |
| Vector_PendantMagnetic_55_16°_2700K_DALI_BrushedBronze_AP31120 | 2700 | 132 mm | Brushed Bronze | 1492 | Artemide_Aluminum_Black | Artemide_Aluminum_BrushedBronze | Artemide_Aluminum_BrushedBronze | Artemide_Aluminum_Black | 1492 | 130 | 55 | AP31120 | 28 mm | 50000 | 26 |
| Vector_PendantMagnetic_55_16°_3000K_DALI_BrushedBronze_AP30120 | 3000 | 132 mm | Brushed Bronze | 1492 | Artemide_Aluminum_Black | Artemide_Aluminum_BrushedBronze | Artemide_Aluminum_BrushedBronze | Artemide_Aluminum_Black | 1492 | 130 | 55 | AP30120 | 28 mm | 50000 | 26 |
| Vector_PendantMagnetic_55_16°_4000K_DALI_BrushedBronze_AP35120 | 4000 | 132 mm | Brushed Bronze | 1492 | Artemide_Aluminum_Black | Artemide_Aluminum_BrushedBronze | Artemide_Aluminum_BrushedBronze | Artemide_Aluminum_Black | 1492 | 130 | 55 | AP35120 | 28 mm | 50000 | 26 |
| Vector_PendantMagnetic_55_22°_2700K_DALI_BrushedBronze_AP31220 | 2700 | 132 mm | Brushed Bronze | 1465 | Artemide_Aluminum_Black | Artemide_Aluminum_BrushedBronze | Artemide_Aluminum_BrushedBronze | Artemide_Aluminum_Black | 1465 | 130 | 55 | AP31220 | 28 mm | 50000 | 26 |
| Vector_PendantMagnetic_55_22°_3000K_DALI_BrushedBronze_AP30220 | 3000 | 132 mm | Brushed Bronze | 1465 | Artemide_Aluminum_Black | Artemide_Aluminum_BrushedBronze | Artemide_Aluminum_BrushedBronze | Artemide_Aluminum_Black | 1465 | 130 | 55 | AP30220 | 28 mm | 50000 | 26 |
| Vector_PendantMagnetic_55_22°_4000K_DALI_BrushedBronze_AP35220 | 4000 | 132 mm | Brushed Bronze | 1465 | Artemide_Aluminum_Black | Artemide_Aluminum_BrushedBronze | Artemide_Aluminum_BrushedBronze | Artemide_Aluminum_Black | 1465 | 130 | 55 | AP35220 | 28 mm | 50000 | 26 |
| Vector_PendantMagnetic_55_32°_2700K_DALI_BrushedBronze_AP31320 | 2700 | 132 mm | Brushed Bronze | 1596 | Artemide_Aluminum_Black | Artemide_Aluminum_BrushedBronze | Artemide_Aluminum_BrushedBronze | Artemide_Aluminum_Black | 1596 | 130 | 55 | AP31320 | 28 mm | 50000 | 26 |
| Vector_PendantMagnetic_55_32°_3000K_DALI_BrushedBronze_AP30320 | 3000 | 132 mm | Brushed Bronze | 1596 | Artemide_Aluminum_Black | Artemide_Aluminum_BrushedBronze | Artemide_Aluminum_BrushedBronze | Artemide_Aluminum_Black | 1596 | 130 | 55 | AP30320 | 28 mm | 50000 | 26 |
| Vector_PendantMagnetic_55_32°_4000K_DALI_BrushedBronze_AP35320 | 4000 | 132 mm | Brushed Bronze | 1596 | Artemide_Aluminum_Black | Artemide_Aluminum_BrushedBronze | Artemide_Aluminum_BrushedBronze | Artemide_Aluminum_Black | 1596 | 130 | 55 | AP35320 | 28 mm | 50000 | 26 |
| Vector_PendantMagnetic_55_16°_2700K_DALI_Black_AP31104 | 2700 | 132 mm | Black | 1492 | Artemide_Aluminum_Black | Artemide_Aluminum_Black | Artemide_Aluminum_Black | Artemide_Aluminum_Black | 1492 | 130 | 55 | AP31104 | 28 mm | 50000 | 26 |
| Vector_PendantMagnetic_55_16°_3000K_DALI_Black_AP30104 | 3000 | 132 mm | Black | 1492 | Artemide_Aluminum_Black | Artemide_Aluminum_Black | Artemide_Aluminum_Black | Artemide_Aluminum_Black | 1492 | 130 | 55 | AP30104 | 28 mm | 50000 | 26 |
| Vector_PendantMagnetic_55_16°_4000K_DALI_Black_AP35104 | 4000 | 132 mm | Black | 1492 | Artemide_Aluminum_Black | Artemide_Aluminum_Black | Artemide_Aluminum_Black | Artemide_Aluminum_Black | 1492 | 130 | 55 | AP35104 | 28 mm | 50000 | 26 |
| Vector_PendantMagnetic_55_22°_2700K_DALI_Black_AP31204 | 2700 | 132 mm | Black | 1465 | Artemide_Aluminum_Black | Artemide_Aluminum_Black | Artemide_Aluminum_Black | Artemide_Aluminum_Black | 1465 | 130 | 55 | AP31204 | 28 mm | 50000 | 26 |
| Vector_PendantMagnetic_55_22°_3000K_DALI_Black_AP30204 | 3000 | 132 mm | Black | 1465 | Artemide_Aluminum_Black | Artemide_Aluminum_Black | Artemide_Aluminum_Black | Artemide_Aluminum_Black | 1465 | 130 | 55 | AP30204 | 28 mm | 50000 | 26 |
| Vector_PendantMagnetic_55_22°_4000K_DALI_Black_AP35204 | 4000 | 132 mm | Black | 1465 | Artemide_Aluminum_Black | Artemide_Aluminum_Black | Artemide_Aluminum_Black | Artemide_Aluminum_Black | 1465 | 130 | 55 | AP35204 | 28 mm | 50000 | 26 |
| Vector_PendantMagnetic_55_32°_2700K_DALI_Black_AP31304 | 2700 | 132 mm | Black | 1596 | Artemide_Aluminum_Black | Artemide_Aluminum_Black | Artemide_Aluminum_Black | Artemide_Aluminum_Black | 1596 | 130 | 55 | AP31304 | 28 mm | 50000 | 26 |
| Vector_PendantMagnetic_55_32°_3000K_DALI_Black_AP30304 | 3000 | 132 mm | Black | 1596 | Artemide_Aluminum_Black | Artemide_Aluminum_Black | Artemide_Aluminum_Black | Artemide_Aluminum_Black | 1596 | 130 | 55 | AP30304 | 28 mm | 50000 | 26 |
| Vector_PendantMagnetic_55_32°_4000K_DALI_Black_AP35304 | 4000 | 132 mm | Black | 1596 | Artemide_Aluminum_Black | Artemide_Aluminum_Black | Artemide_Aluminum_Black | Artemide_Aluminum_Black | 1596 | 130 | 55 | AP35304 | 28 mm | 50000 | 26 |
| Vector_PendantMagnetic_55_16°_2700K_DALI_BrushedCopper_AP31118 | 2700 | 132 mm | Brushed Copper | 1492 | Artemide_Aluminum_Black | Artemide_Aluminum_BrushedCopper | Artemide_Aluminum_BrushedCopper | Artemide_Aluminum_Black | 1492 | 130 | 55 | AP31118 | 28 mm | 50000 | 26 |
| Vector_PendantMagnetic_55_16°_3000K_DALI_BrushedCopper_AP30118 | 3000 | 132 mm | Brushed Copper | 1492 | Artemide_Aluminum_Black | Artemide_Aluminum_BrushedCopper | Artemide_Aluminum_BrushedCopper | Artemide_Aluminum_Black | 1492 | 130 | 55 | AP30118 | 28 mm | 50000 | 26 |
| Vector_PendantMagnetic_55_16°_4000K_DALI_BrushedCopper_AP35118 | 4000 | 132 mm | Brushed Copper | 1492 | Artemide_Aluminum_Black | Artemide_Aluminum_BrushedCopper | Artemide_Aluminum_BrushedCopper | Artemide_Aluminum_Black | 1492 | 130 | 55 | AP35118 | 28 mm | 50000 | 26 |
| Vector_PendantMagnetic_55_22°_2700K_DALI_BrushedCopper_AP31218 | 2700 | 132 mm | Brushed Copper | 1465 | Artemide_Aluminum_Black | Artemide_Aluminum_BrushedCopper | Artemide_Aluminum_BrushedCopper | Artemide_Aluminum_Black | 1465 | 130 | 55 | AP31218 | 28 mm | 50000 | 26 |
| Vector_PendantMagnetic_55_22°_3000K_DALI_BrushedCopper_AP30218 | 3000 | 132 mm | Brushed Copper | 1465 | Artemide_Aluminum_Black | Artemide_Aluminum_BrushedCopper | Artemide_Aluminum_BrushedCopper | Artemide_Aluminum_Black | 1465 | 130 | 55 | AP30218 | 28 mm | 50000 | 26 |
| Vector_PendantMagnetic_55_22°_4000K_DALI_BrushedCopper_AP35218 | 4000 | 132 mm | Brushed Copper | 1465 | Artemide_Aluminum_Black | Artemide_Aluminum_BrushedCopper | Artemide_Aluminum_BrushedCopper | Artemide_Aluminum_Black | 1465 | 130 | 55 | AP35218 | 28 mm | 50000 | 26 |
| Vector_PendantMagnetic_55_32°_2700K_DALI_BrushedCopper_AP31318 | 2700 | 132 mm | Brushed Copper | 1596 | Artemide_Aluminum_Black | Artemide_Aluminum_BrushedCopper | Artemide_Aluminum_BrushedCopper | Artemide_Aluminum_Black | 1596 | 130 | 55 | AP31318 | 28 mm | 50000 | 26 |
| Vector_PendantMagnetic_55_32°_3000K_DALI_BrushedCopper_AP30318 | 3000 | 132 mm | Brushed Copper | 1596 | Artemide_Aluminum_Black | Artemide_Aluminum_BrushedCopper | Artemide_Aluminum_BrushedCopper | Artemide_Aluminum_Black | 1596 | 130 | 55 | AP30318 | 28 mm | 50000 | 26 |
| Vector_PendantMagnetic_55_32°_4000K_DALI_BrushedCopper_AP35318 | 4000 | 132 mm | Brushed Copper | 1596 | Artemide_Aluminum_Black | Artemide_Aluminum_BrushedCopper | Artemide_Aluminum_BrushedCopper | Artemide_Aluminum_Black | 1596 | 130 | 55 | AP35318 | 28 mm | 50000 | 26 |

note: [stored X ft] marks values corroborated as IEEE doubles in the binary element streams (Revit-internal decimal feet)

## geometry (parser evidence)
native form markers: Sweep x6
no freeform markers — native parametric forms only
